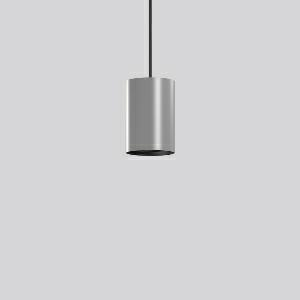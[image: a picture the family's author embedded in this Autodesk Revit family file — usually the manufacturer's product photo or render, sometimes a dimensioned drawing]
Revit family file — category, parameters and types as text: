
# Revit family: deecos_p_maxi_911531_004_5758
name_source: partatom
category: Lighting Fixtures
units: mm (PartAtom-declared; Revit-internal decimal feet)

## family parameters
Cut with Voids When Loaded = No
Host = Face
Light Source = No
Part Type = Normal
Room Calculation Point = No
Round Connector Dimension = Use Diameter
Shared = No

## types (1)
- DEECOS P maxi (1 x LED Modul 930, 3350 lm, 3000)
    Apparent Load = 25 VA
    Approval mark = CE
    CIE Flux Codes = 100 100 100 100 100
    Color Rendering = 90
    Color Temperature = 3000
    Default Elevation = 1800 mm
    Description = Series: DEECOS P maxi
Cylindrical pendant luminaire. Housing: die-cast aluminium, powder-coated. Canopy made of powder-coated sheet steel with magnetic attachment. Optical assembly with reflector made of MIRO-Silver with 98% total light reflection for outstanding efficiency - can be changed without tools. Best colour rendering index Ra>90. Transparent suspension cable 2 m, can be shortened. High quality converter without flickering and stroboscopic effect. The following accessories can be mounted without use of tools: interchangeable lenses, honeycomb louvre, clear and frosted diffusers, white interchangeable plastic ring. Decorative recessed suspension set available as accessory. 
Colour: silver
Diameter: 123 mm
Height: 181 mm
Suspension length: 2000 mm
Lamp: LED
Socket: without socket
Colour temperature: 3000K
Colour rendering index (CRI): 92
System power: 25 W
Rated luminous flux: 3350 lm
Luminous efficiency: 134 lm/W
Control gear: Regulated power supply
Protection class: I
Type of protection: IP 20
    Height = 181 mm
    Lamp = 1 x LED Modul 930
    Lamp Light Flux = 3350 lm
    Lamp count = 1
    Length = 123 mm
    Lifetime = 50000 h
    Luminous efficacy = 134 lm/W
    Manufacturer = RZB
    ModVariant = No
    Model = 911531.004
    Mounting Place = Ceiling
    Mounting Type = Pendant
    Number of Poles = 1
    OnlyDefault = Yes
    Power Factor = 1
    Product Name = DEECOS P maxi
    Product group = Pendant luminaires
    ProductGroupID = 902
    Protection Class = Protection class I
    Protection Degree = IP 20
    RLX_Detail_Level = 1
    RLX_Emergency_Light_Flux = 0 lm
    RLX_Emergency_Type = 0
    RLX_Emergency_Type_DB = No
    RlxData = <blob elided: 36009 chars, md5=3d2909a4>
    Socket = socket
    Standby Power = 0 W
    System Light Flux = 3350 lm
    System Power = 25 W
    Type Comments = Product without accessories
    Type Image = 911480.004.jpg
    URL = http://relux.com
    VarID = ---
    Voltage = 230 V
    Voltage Range = 220-240 V
    Weight = 0.00 kg
    Width = 0 mm  [stored 0 ft]

note: [stored X ft] marks values corroborated as IEEE doubles in the binary element streams (Revit-internal decimal feet)

## geometry (parser evidence)
native form markers: Blend x4, Sweep x8
no freeform markers — native parametric forms only
